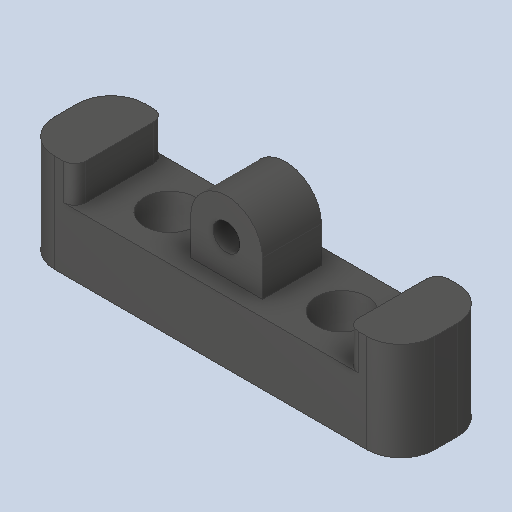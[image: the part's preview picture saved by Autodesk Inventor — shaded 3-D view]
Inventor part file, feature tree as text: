
AUTODESK INVENTOR PART (.ipt)
format: ipt  version: 2023.4 (Build 274418000, 418)  size: 122,368 bytes
history: native  units: in
note: dims shown in document units (in); Inventor stores cm internally (conversion verified against a paired STEP export)
features: fillet x1
ambient origin geometry x8: Origin, YZ Plane, XZ Plane, XY Plane, X Axis, Y Axis, Z Axis, Center Point
bodies: Solid1 (feature_tree)
feature tree (1):
  fillet  "Fillet2"  [1 undecoded]
note: 1 required parameter value undecoded (feature->parameter linkage not recoverable at this tier; creation-order binding heuristic only, values carry confidence <= 0.55)
